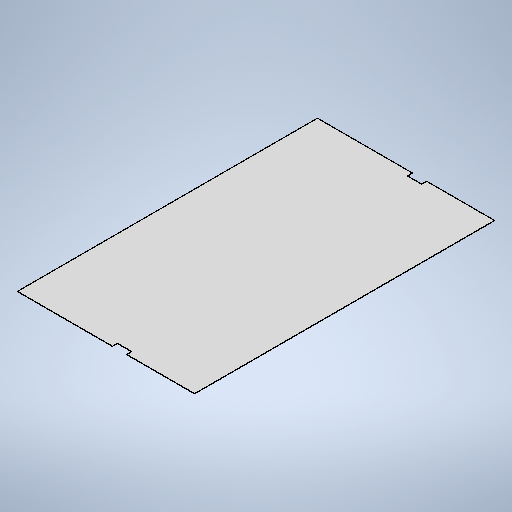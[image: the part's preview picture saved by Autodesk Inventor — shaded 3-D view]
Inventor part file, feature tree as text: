
AUTODESK INVENTOR PART (.ipt)
format: ipt  version: 2025.3 (Build 293356000, 356)  size: 295,936 bytes
history: native  units: mm
features: other x3, sketch x2, sheet_metal_op x1
ambient origin geometry x8: Origin, YZ Plane, XZ Plane, XY Plane, X Axis, Y Axis, Z Axis, Center Point
bodies: Solid1 (feature_tree)
feature tree (6):
  sheet_metal_op  "Face1"
  sketch  "Sketch1"  dims[d2=3.0mm]
  other  "Plate1"
  sketch  "Sketch5"  dims[d22=1240.0mm d23=2100.0mm d24=65.0mm d25=35.0mm d28=100.0mm d29=410.0mm d30=100.0mm d31=2.0mm d32=5.0mm d33=4.0mm d34=0.5mm d35=5.0mm d36=5.0mm d37=5.0mm d38=2.0mm d39=3.0mm d40=0.0mm]
  other  "Cut1"
  other  "Definition1"
